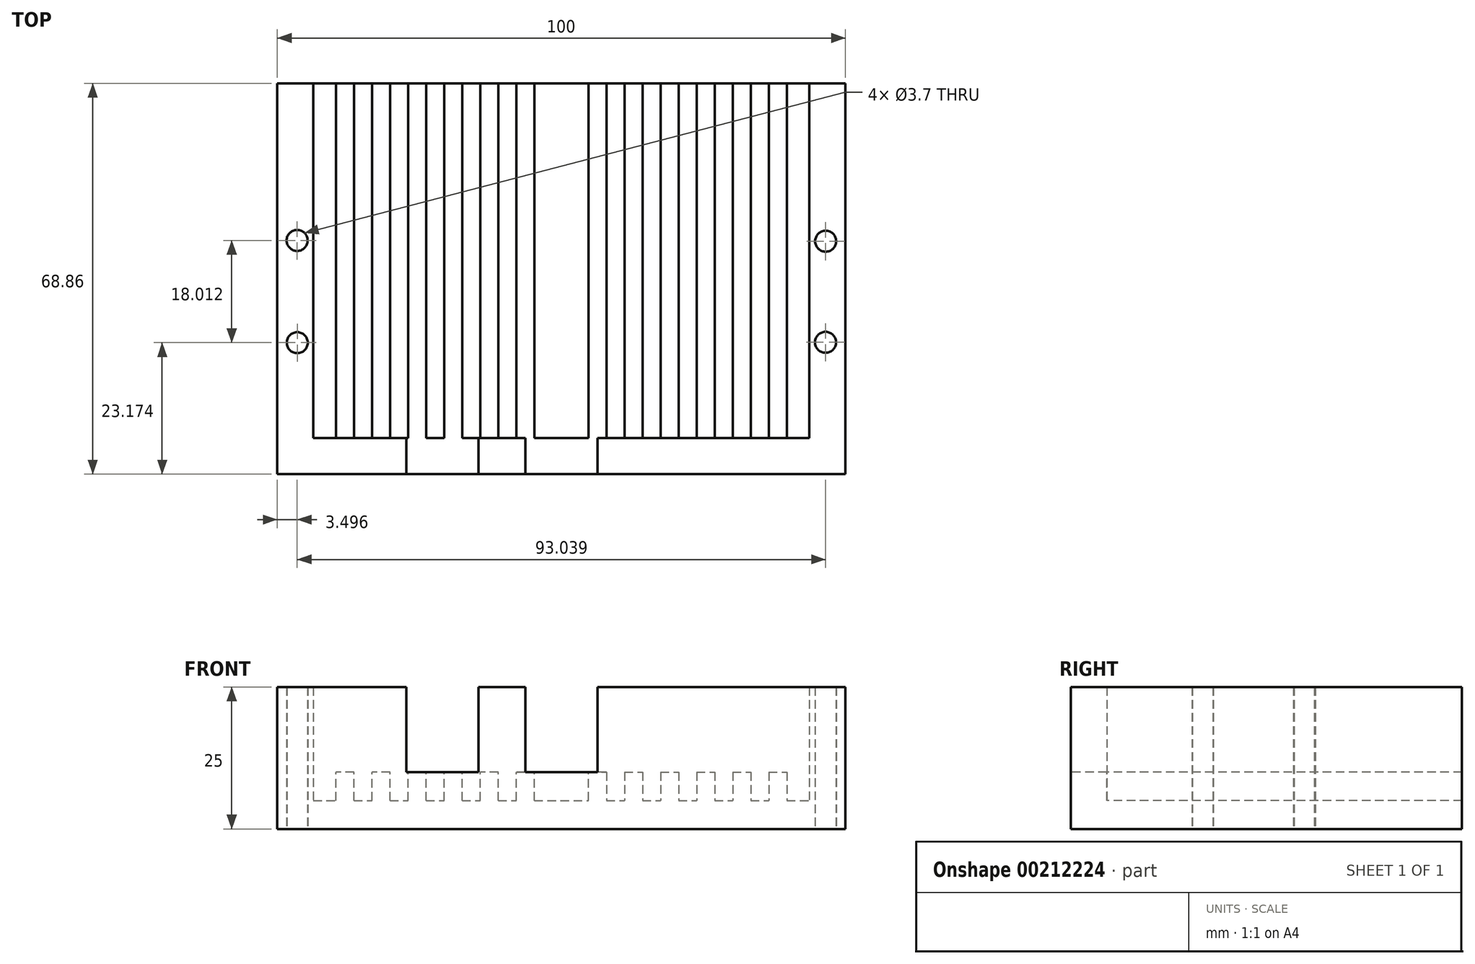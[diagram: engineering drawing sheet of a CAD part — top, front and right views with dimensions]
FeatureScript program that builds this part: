
annotation { "Feature Type Name" : "Feature", "Feature Type Description" : "" }
export const myFeature = defineFeature(function(context is Context, id is Id, definition is map)
    precondition{}
    {
        {
            var Q0;
            Q0=qCreatedBy(makeId("Top.planeOp"),FACE);
            var sketch = newSketch(context, id + "F0", { "sketchPlane" : qUnion([Q0])});
            skLineSegment(sketch, "E0.bottom", {"start": v(-44.9, -50.75) * mm, "end": v(55.1, -50.75) * mm});
            skLineSegment(sketch, "E0.top", {"start": v(-44.9, 18.1) * mm, "end": v(55.1, 18.1) * mm});
            skLineSegment(sketch, "E0.left", {"start": v(-44.9, -50.75) * mm, "end": v(-44.9, 18.1) * mm});
            skLineSegment(sketch, "E0.right", {"start": v(55.1, -50.75) * mm, "end": v(55.1, 18.1) * mm});
            skPoint(sketch, "E1.endSnap0", {"position": v(4.98, -50.77) * mm});
            skSolve(sketch);
        }
        {
            var Q0;
            Q0=qSketchRegion(id+"F0",true);
            extrude(context, id + "F1", {"entities" : qUnion([Q0]), "oppositeDirection" : true, "depth" : 5 * mm});
        }
        {
            var Q0;
            Q0=makeQuery(id+"F1.opExtrude","CAP_FACE",FACE,{"disambiguationData":[OSD([sQuery(id+"F0.wireOp",EDGE,"E0.bottom"),sQuery(id+"F0.wireOp",EDGE,"E0.top"),sQuery(id+"F0.wireOp",EDGE,"E0.left"),sQuery(id+"F0.wireOp",EDGE,"E0.right")])],"isStart":true});
            var sketch = newSketch(context, id + "F2", { "sketchPlane" : qUnion([Q0])});
            skLineSegment(sketch, "E2.bottom", {"start": v(-34.58, 18.1) * mm, "end": v(-31.4, 18.1) * mm});
            skLineSegment(sketch, "E2.top", {"start": v(-34.58, -50.75) * mm, "end": v(-31.4, -50.75) * mm});
            skLineSegment(sketch, "E2.left", {"start": v(-34.58, 18.1) * mm, "end": v(-34.58, -50.75) * mm});
            skLineSegment(sketch, "E2.right", {"start": v(-31.4, 18.1) * mm, "end": v(-31.4, -50.75) * mm});
            skLineSegment(sketch, "E3", {"start": v(-31.4, 18.1) * mm, "end": v(-28.23, 18.1) * mm});
            skLineSegment(sketch, "E4.1.0.0", {"start": v(-25.06, 18.1) * mm, "end": v(-25.06, -50.75) * mm});
            skLineSegment(sketch, "E4.1.0.1", {"start": v(-28.23, 18.1) * mm, "end": v(-25.06, 18.1) * mm});
            skLineSegment(sketch, "E4.1.0.2", {"start": v(-28.23, 18.1) * mm, "end": v(-28.23, -50.75) * mm});
            skLineSegment(sketch, "E4.1.0.3", {"start": v(-28.23, -50.75) * mm, "end": v(-25.06, -50.75) * mm});
            skLineSegment(sketch, "E4.2.0.0", {"start": v(-18.7, 18.1) * mm, "end": v(-18.7, -50.75) * mm});
            skLineSegment(sketch, "E4.2.0.1", {"start": v(-21.88, 18.1) * mm, "end": v(-18.7, 18.1) * mm});
            skLineSegment(sketch, "E4.2.0.2", {"start": v(-21.88, 18.1) * mm, "end": v(-21.88, -50.75) * mm});
            skLineSegment(sketch, "E4.2.0.3", {"start": v(-21.88, -50.75) * mm, "end": v(-18.7, -50.75) * mm});
            skLineSegment(sketch, "E4.direction1", {"start": v(-31.4, -50.75) * mm, "end": v(-25.06, -50.75) * mm, "construction": true});
            skLineSegment(sketch, "E5.0.3.0", {"start": v(-12.36, 18.1) * mm, "end": v(-12.36, -50.75) * mm});
            skLineSegment(sketch, "E5.3.3.0", {"start": v(-15.53, 18.1) * mm, "end": v(-12.36, 18.1) * mm});
            skLineSegment(sketch, "E5.6.3.0", {"start": v(-15.53, 18.1) * mm, "end": v(-15.53, -50.75) * mm});
            skLineSegment(sketch, "E5.9.3.0", {"start": v(-15.53, -50.75) * mm, "end": v(-12.36, -50.75) * mm});
            skLineSegment(sketch, "E5.0.4.0", {"start": v(-6, 18.1) * mm, "end": v(-6, -50.75) * mm});
            skLineSegment(sketch, "E5.3.4.0", {"start": v(-9.18, 18.1) * mm, "end": v(-6, 18.1) * mm});
            skLineSegment(sketch, "E5.6.4.0", {"start": v(-9.18, 18.1) * mm, "end": v(-9.18, -50.75) * mm});
            skLineSegment(sketch, "E5.9.4.0", {"start": v(-9.18, -50.75) * mm, "end": v(-6, -50.75) * mm});
            skLineSegment(sketch, "E5.0.5.0", {"start": v(0.34, 18.1) * mm, "end": v(0.34, -50.75) * mm});
            skLineSegment(sketch, "E5.3.5.0", {"start": v(-2.83, 18.1) * mm, "end": v(0.34, 18.1) * mm});
            skLineSegment(sketch, "E5.6.5.0", {"start": v(-2.83, 18.1) * mm, "end": v(-2.83, -50.75) * mm});
            skLineSegment(sketch, "E5.9.5.0", {"start": v(-2.83, -50.75) * mm, "end": v(0.34, -50.75) * mm});
            skLineSegment(sketch, "E5.0.7.0", {"start": v(13.04, 18.1) * mm, "end": v(13.04, -50.75) * mm});
            skLineSegment(sketch, "E5.3.7.0", {"start": v(9.87, 18.1) * mm, "end": v(13.04, 18.1) * mm});
            skLineSegment(sketch, "E5.6.7.0", {"start": v(9.87, 18.1) * mm, "end": v(9.87, -50.75) * mm});
            skLineSegment(sketch, "E5.9.7.0", {"start": v(9.87, -50.75) * mm, "end": v(13.04, -50.75) * mm});
            skLineSegment(sketch, "E5.0.8.0", {"start": v(19.4, 18.1) * mm, "end": v(19.4, -50.75) * mm});
            skLineSegment(sketch, "E5.3.8.0", {"start": v(16.22, 18.1) * mm, "end": v(19.4, 18.1) * mm});
            skLineSegment(sketch, "E5.6.8.0", {"start": v(16.22, 18.1) * mm, "end": v(16.22, -50.75) * mm});
            skLineSegment(sketch, "E5.9.8.0", {"start": v(16.22, -50.75) * mm, "end": v(19.4, -50.75) * mm});
            skLineSegment(sketch, "E5.0.9.0", {"start": v(25.74, 18.1) * mm, "end": v(25.74, -50.75) * mm});
            skLineSegment(sketch, "E5.3.9.0", {"start": v(22.57, 18.1) * mm, "end": v(25.74, 18.1) * mm});
            skLineSegment(sketch, "E5.6.9.0", {"start": v(22.57, 18.1) * mm, "end": v(22.57, -50.75) * mm});
            skLineSegment(sketch, "E5.9.9.0", {"start": v(22.57, -50.75) * mm, "end": v(25.74, -50.75) * mm});
            skLineSegment(sketch, "E5.0.10.0", {"start": v(32.1, 18.1) * mm, "end": v(32.1, -50.75) * mm});
            skLineSegment(sketch, "E5.3.10.0", {"start": v(28.92, 18.1) * mm, "end": v(32.1, 18.1) * mm});
            skLineSegment(sketch, "E5.6.10.0", {"start": v(28.92, 18.1) * mm, "end": v(28.92, -50.75) * mm});
            skLineSegment(sketch, "E5.9.10.0", {"start": v(28.92, -50.75) * mm, "end": v(32.1, -50.75) * mm});
            skLineSegment(sketch, "E5.0.11.0", {"start": v(38.44, 18.1) * mm, "end": v(38.44, -50.75) * mm});
            skLineSegment(sketch, "E5.3.11.0", {"start": v(35.27, 18.1) * mm, "end": v(38.44, 18.1) * mm});
            skLineSegment(sketch, "E5.6.11.0", {"start": v(35.27, 18.1) * mm, "end": v(35.27, -50.75) * mm});
            skLineSegment(sketch, "E5.9.11.0", {"start": v(35.27, -50.75) * mm, "end": v(38.44, -50.75) * mm});
            skLineSegment(sketch, "E5.0.12.0", {"start": v(44.8, 18.1) * mm, "end": v(44.8, -50.75) * mm});
            skLineSegment(sketch, "E5.3.12.0", {"start": v(41.62, 18.1) * mm, "end": v(44.8, 18.1) * mm});
            skLineSegment(sketch, "E5.6.12.0", {"start": v(41.62, 18.1) * mm, "end": v(41.62, -50.75) * mm});
            skLineSegment(sketch, "E5.9.12.0", {"start": v(41.62, -50.75) * mm, "end": v(44.8, -50.75) * mm});
            skSolve(sketch);
        }
        {
            var Q0;
            Q0 = qSketchRegion(id + "F2", true);
            extrude(context, id + "F3", {"entities" : qUnion([Q0]), "operationType" : NewBodyOperationType.ADD, "depth" : 5 * mm});
        }
        {
            var Q0;
            {var subQ0=sQuery(id+"F0.wireOp",EDGE,"E0.top");var subQ1=sQuery(id+"F0.wireOp",EDGE,"E0.bottom");Q0=makeQuery(id+"F3.boolean.opBoolean","SPLIT",FACE,{"disambiguationData":[TD([makeQuery(id+"F3.opExtrude","SWEPT_FACE",FACE,{"disambiguationData":[OSD([sQuery(id+"F2.wireOp",EDGE,"E5.0.5.0")])]})])],"derivedFrom":makeQuery(id+"F1.opExtrude","CAP_FACE",FACE,{"disambiguationData":[OSD([subQ1,subQ0,sQuery(id+"F0.wireOp",EDGE,"E0.left"),sQuery(id+"F0.wireOp",EDGE,"E0.right")])],"isStart":true})});}
            var sketch = newSketch(context, id + "F4", { "sketchPlane" : qUnion([Q0])});
            skLineSegment(sketch, "E6.bottom", {"start": v(-44.9, 18.1) * mm, "end": v(-38.56, 18.1) * mm});
            skLineSegment(sketch, "E6.top", {"start": v(-44.9, -50.75) * mm, "end": v(-38.56, -50.75) * mm});
            skLineSegment(sketch, "E6.left", {"start": v(-44.9, 18.1) * mm, "end": v(-44.9, -50.75) * mm});
            skLineSegment(sketch, "E6.right", {"start": v(-38.56, 18.1) * mm, "end": v(-38.56, -50.75) * mm});
            skPoint(sketch, "E7", {"position": v(55.1, 18.1) * mm});
            skLineSegment(sketch, "E8.bottom", {"start": v(55.1, 18.1) * mm, "end": v(48.74, 18.1) * mm});
            skLineSegment(sketch, "E8.top", {"start": v(55.1, -50.75) * mm, "end": v(48.74, -50.75) * mm});
            skLineSegment(sketch, "E8.left", {"start": v(55.1, 18.1) * mm, "end": v(55.1, -50.75) * mm});
            skLineSegment(sketch, "E8.right", {"start": v(48.74, 18.1) * mm, "end": v(48.74, -50.75) * mm});
            skPoint(sketch, "E9", {"position": v(-44.9, -50.75) * mm});
            skLineSegment(sketch, "E10.bottom", {"start": v(-44.9, -50.75) * mm, "end": v(55.1, -50.75) * mm});
            skLineSegment(sketch, "E10.top", {"start": v(-44.9, -44.4) * mm, "end": v(55.1, -44.4) * mm});
            skLineSegment(sketch, "E10.left", {"start": v(-44.9, -50.75) * mm, "end": v(-44.9, -44.4) * mm});
            skLineSegment(sketch, "E10.right", {"start": v(55.1, -50.75) * mm, "end": v(55.1, -44.4) * mm});
            skPoint(sketch, "E11", {"position": v(-44.9, 18.1) * mm});
            skSolve(sketch);
        }
        {
            var Q0;
            Q0 = qSketchRegion(id + "F4", true);
            extrude(context, id + "F5", {"entities" : qUnion([Q0]), "operationType" : NewBodyOperationType.ADD, "depth" : 20 * mm});
        }
        {
            var Q0;
            Q0=makeQuery(id+"F1.boolean.opBoolean","MERGE",FACE,{"derivedFrom":[makeQuery(id+"FrM0S1BdwquSU4h_1.opExtrude","CAP_FACE",FACE,{"disambiguationData":[OSD([sQuery(id+"F1paRBLzH6P92U9_1.wireOp",EDGE,"ca1a8222-2888-463a-b1ca-637cd0208124.0"),sQuery(id+"F1paRBLzH6P92U9_1.wireOp",EDGE,"ca1a8222-2888-463a-b1ca-637cd0208124.1"),sQuery(id+"F1paRBLzH6P92U9_1.wireOp",EDGE,"ca1a8222-2888-463a-b1ca-637cd0208124.2"),sQuery(id+"F1paRBLzH6P92U9_1.wireOp",EDGE,"ca1a8222-2888-463a-b1ca-637cd0208124.3")])],"isStart":true}),makeQuery(id+"F1.opExtrude","CAP_FACE",FACE,{"disambiguationData":[OSD([sQuery(id+"F0.wireOp",EDGE,"E0.bottom"),sQuery(id+"F0.wireOp",EDGE,"E0.top"),sQuery(id+"F0.wireOp",EDGE,"E0.left"),sQuery(id+"F0.wireOp",EDGE,"E0.right")])],"isStart":false})]});
            var sketch = newSketch(context, id + "F6", { "sketchPlane" : qUnion([Q0])});
            skCircle(sketch, "E12", {"center": v(-41.39, 27.58) * mm, "radius": 1.85 * mm});
            skCircle(sketch, "E13", {"center": v(51.6, 27.51) * mm, "radius": 1.85 * mm});
            skLineSegment(sketch, "E14", {"start": v(-44.9, 50.75) * mm, "end": v(-41.4, 50.75) * mm});
            skCircle(sketch, "E15", {"center": v(-41.41, 9.56) * mm, "radius": 1.85 * mm});
            skCircle(sketch, "E16", {"center": v(51.62, 9.7) * mm, "radius": 1.85 * mm});
            skSolve(sketch);
        }
        {
            var Q0;
            Q0=qSketchRegion(id+"F6",true);
            extrude(context, id + "F7", {"entities" : qUnion([Q0]), "operationType" : NewBodyOperationType.REMOVE, "endBound" : BoundingType.THROUGH_ALL, "oppositeDirection" : true, "depth" : 25.4 * mm});
        }
        {
            var Q0;
            Q0=makeQuery(id+"F5.boolean.opBoolean","MERGE",FACE,{"derivedFrom":[makeQuery(id+"F3.boolean.opBoolean","MERGE",FACE,{"derivedFrom":[makeQuery(id+"F1.opExtrude","SWEPT_FACE",FACE,{"disambiguationData":[OSD([sQuery(id+"F0.wireOp",EDGE,"E0.bottom")])]}),makeQuery(id+"F3.opExtrude","SWEPT_FACE",FACE,{"disambiguationData":[OSD([sQuery(id+"F2.wireOp",EDGE,"E2.top")])]}),makeQuery(id+"F3.opExtrude","SWEPT_FACE",FACE,{"disambiguationData":[OSD([sQuery(id+"F2.wireOp",EDGE,"E4.1.0.3")])]}),makeQuery(id+"F3.opExtrude","SWEPT_FACE",FACE,{"disambiguationData":[OSD([sQuery(id+"F2.wireOp",EDGE,"E4.2.0.3")])]}),makeQuery(id+"F3.opExtrude","SWEPT_FACE",FACE,{"disambiguationData":[OSD([sQuery(id+"F2.wireOp",EDGE,"E5.9.3.0")])]}),makeQuery(id+"F3.opExtrude","SWEPT_FACE",FACE,{"disambiguationData":[OSD([sQuery(id+"F2.wireOp",EDGE,"E5.9.4.0")])]}),makeQuery(id+"F3.opExtrude","SWEPT_FACE",FACE,{"disambiguationData":[OSD([sQuery(id+"F2.wireOp",EDGE,"E5.9.5.0")])]}),makeQuery(id+"F3.opExtrude","SWEPT_FACE",FACE,{"disambiguationData":[OSD([sQuery(id+"F2.wireOp",EDGE,"E5.9.7.0")])]}),makeQuery(id+"F3.opExtrude","SWEPT_FACE",FACE,{"disambiguationData":[OSD([sQuery(id+"F2.wireOp",EDGE,"E5.9.8.0")])]}),makeQuery(id+"F3.opExtrude","SWEPT_FACE",FACE,{"disambiguationData":[OSD([sQuery(id+"F2.wireOp",EDGE,"E5.9.9.0")])]}),makeQuery(id+"F3.opExtrude","SWEPT_FACE",FACE,{"disambiguationData":[OSD([sQuery(id+"F2.wireOp",EDGE,"E5.9.10.0")])]}),makeQuery(id+"F3.opExtrude","SWEPT_FACE",FACE,{"disambiguationData":[OSD([sQuery(id+"F2.wireOp",EDGE,"E5.9.11.0")])]}),makeQuery(id+"F3.opExtrude","SWEPT_FACE",FACE,{"disambiguationData":[OSD([sQuery(id+"F2.wireOp",EDGE,"E5.9.12.0")])]})]}),makeQuery(id+"F5.opExtrude","SWEPT_FACE",FACE,{"disambiguationData":[OSD([sQuery(id+"F4.wireOp",EDGE,"E10.bottom")])]})]});
            var sketch = newSketch(context, id + "F8", { "sketchPlane" : qUnion([Q0])});
            skLineSegment(sketch, "E17", {"start": v(5.1, 5) * mm, "end": v(-1.26, 5) * mm});
            skLineSegment(sketch, "E18", {"start": v(5.1, 5) * mm, "end": v(11.44, 5) * mm});
            skLineSegment(sketch, "E19", {"start": v(11.44, 5) * mm, "end": v(11.44, 20) * mm});
            skLineSegment(sketch, "E20", {"start": v(-1.26, 5) * mm, "end": v(-1.26, 20) * mm});
            skLineSegment(sketch, "E21", {"start": v(-1.26, 20) * mm, "end": v(11.44, 20) * mm});
            skLineSegment(sketch, "E22.bottom", {"start": v(-1.26, 5) * mm, "end": v(11.44, 5) * mm});
            skLineSegment(sketch, "E22.top", {"start": v(-1.26, 5) * mm, "end": v(11.44, 5) * mm});
            skLineSegment(sketch, "E22.left", {"start": v(-1.26, 5) * mm, "end": v(-1.26, 5) * mm});
            skLineSegment(sketch, "E22.right", {"start": v(11.44, 5) * mm, "end": v(11.44, 5) * mm});
            skLineSegment(sketch, "E23", {"start": v(-22.21, 5) * mm, "end": v(-22.21, 20) * mm});
            skLineSegment(sketch, "E24", {"start": v(-22.21, 5) * mm, "end": v(-9.51, 5) * mm});
            skLineSegment(sketch, "E25", {"start": v(-9.51, 5) * mm, "end": v(-9.51, 20) * mm});
            skLineSegment(sketch, "E26", {"start": v(-9.51, 20) * mm, "end": v(-22.21, 20) * mm});
            skSolve(sketch);
        }
        {
            var Q0;
            Q0 = qSketchRegion(id + "F8", true);
            extrude(context, id + "F9", {"entities" : qUnion([Q0]), "operationType" : NewBodyOperationType.REMOVE, "oppositeDirection" : true, "depth" : 12.7 * mm});
        }
    });
